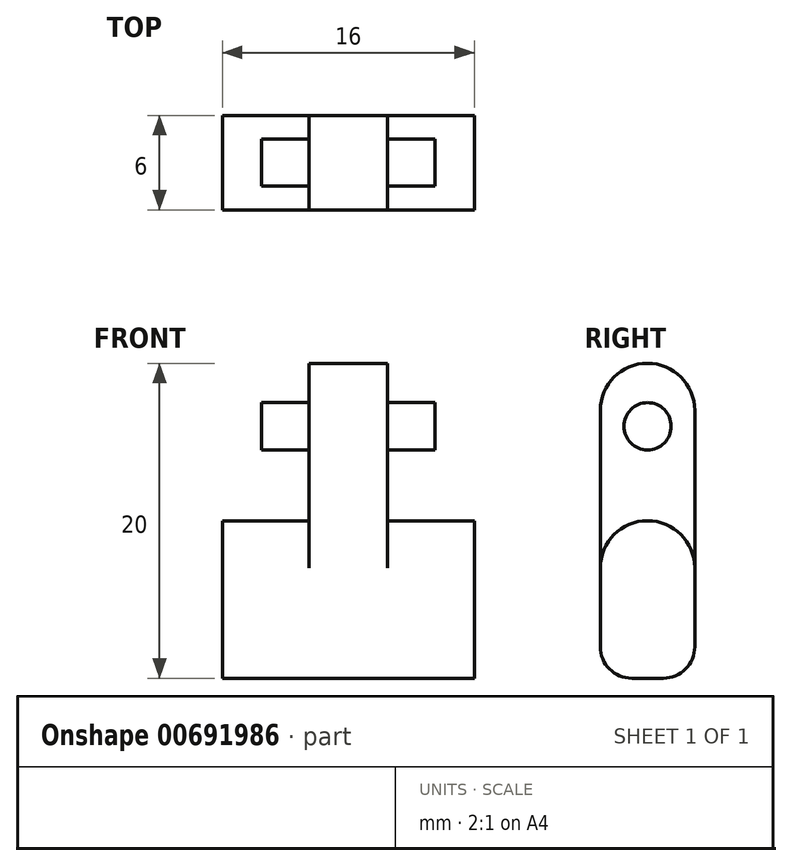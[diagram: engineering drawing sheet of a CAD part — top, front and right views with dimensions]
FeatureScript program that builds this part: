
annotation { "Feature Type Name" : "Feature", "Feature Type Description" : "" }
export const myFeature = defineFeature(function(context is Context, id is Id, definition is map)
    precondition{}
    {
        {
            var Q0;
            Q0=qCreatedBy(makeId("Front.planeOp"),FACE);
            var sketch = newSketch(context, id + "F0", { "sketchPlane" : qUnion([Q0])});
            skLineSegment(sketch, "E0", {"start": v(0, 0) * mm, "end": v(0, -10) * mm});
            skLineSegment(sketch, "E1", {"start": v(0, -10) * mm, "end": v(16, -10) * mm});
            skLineSegment(sketch, "E2", {"start": v(16, -10) * mm, "end": v(16, 0) * mm});
            skLineSegment(sketch, "E3", {"start": v(16, 0) * mm, "end": v(10.5, 0) * mm});
            skLineSegment(sketch, "E4", {"start": v(10.5, 10) * mm, "end": v(10.5, 0) * mm});
            skLineSegment(sketch, "E5", {"start": v(10.5, 10) * mm, "end": v(5.5, 10) * mm});
            skLineSegment(sketch, "E6", {"start": v(5.5, 0) * mm, "end": v(5.5, 10) * mm});
            skLineSegment(sketch, "E7", {"start": v(5.5, 0) * mm, "end": v(0, 0) * mm});
            skSolve(sketch);
        }
        {
            var Q0;
            Q0=makeQuery(id+"F0.imprint","IMPRINT",FACE,{"disambiguationData":[TD([[makeQuery(id+"F0.imprint","IMPRINT",EDGE,{"derivedFrom":sQuery(id+"F0.wireOp",EDGE,"E0")}),1.0]])]});
            extrude(context, id + "F1", {"entities" : qUnion([Q0]), "depth" : 6 * mm, "offsetDistance" : 25 * mm});
        }
        {
            var Q0;
            Q0=makeQuery(id+"F1.opExtrude","SWEPT_FACE",FACE,{"disambiguationData":[OSD([sQuery(id+"F0.wireOp",EDGE,"E4")])]});
            var sketch = newSketch(context, id + "F2", { "sketchPlane" : qUnion([Q0])});
            skCircle(sketch, "E8", {"center": v(-3, 6) * mm, "radius": 1.5 * mm});
            skSolve(sketch);
        }
        {
            var Q0;
            Q0=qSketchRegion(id+"F2",true);
            extrude(context, id + "F3", {"entities" : qUnion([Q0]), "operationType" : NewBodyOperationType.ADD, "depth" : (3) * mm, "offsetDistance" : 25 * mm, "hasSecondDirection" : true, "secondDirectionOppositeDirection" : true, "secondDirectionDepth" : 8 * mm});
        }
        {
            var Q0;
            Q0=makeQuery(id+"F1.opExtrude","CAP_EDGE",EDGE,{"disambiguationData":[OSD([sQuery(id+"F0.wireOp",EDGE,"E5")])],"isStart":false});
            var Q1;
            Q1=makeQuery(id+"F1.opExtrude","CAP_EDGE",EDGE,{"disambiguationData":[OSD([sQuery(id+"F0.wireOp",EDGE,"E5")])],"isStart":true});
            fillet(context, id + "F4", {"entities" : qUnion([Q0, Q1]), "radius" : 3 * mm, "tangentPropagation" : true, "allowEdgeOverflow" : false});
        }
        {
            var Q0;
            Q0=makeQuery(id+"F1.opExtrude","CAP_EDGE",EDGE,{"disambiguationData":[OSD([sQuery(id+"F0.wireOp",EDGE,"E7")])],"isStart":false});
            var Q1;
            Q1=makeQuery(id+"F1.opExtrude","CAP_EDGE",EDGE,{"disambiguationData":[OSD([sQuery(id+"F0.wireOp",EDGE,"E7")])],"isStart":true});
            var Q2;
            Q2=makeQuery(id+"F1.opExtrude","CAP_EDGE",EDGE,{"disambiguationData":[OSD([sQuery(id+"F0.wireOp",EDGE,"E3")])],"isStart":false});
            var Q3;
            Q3=makeQuery(id+"F1.opExtrude","CAP_EDGE",EDGE,{"disambiguationData":[OSD([sQuery(id+"F0.wireOp",EDGE,"E3")])],"isStart":true});
            fillet(context, id + "F5", {"entities" : qUnion([Q0, Q1, Q2, Q3]), "radius" : 3 * mm, "tangentPropagation" : true, "allowEdgeOverflow" : false});
        }
        {
            var Q0;
            Q0=makeQuery(id+"F1.opExtrude","CAP_EDGE",EDGE,{"disambiguationData":[OSD([sQuery(id+"F0.wireOp",EDGE,"E1")])],"isStart":false});
            var Q1;
            Q1=makeQuery(id+"F1.opExtrude","CAP_EDGE",EDGE,{"disambiguationData":[OSD([sQuery(id+"F0.wireOp",EDGE,"E1")])],"isStart":true});
            fillet(context, id + "F6", {"entities" : qUnion([Q0, Q1]), "radius" : 2 * mm, "tangentPropagation" : true, "allowEdgeOverflow" : false});
        }
    });
